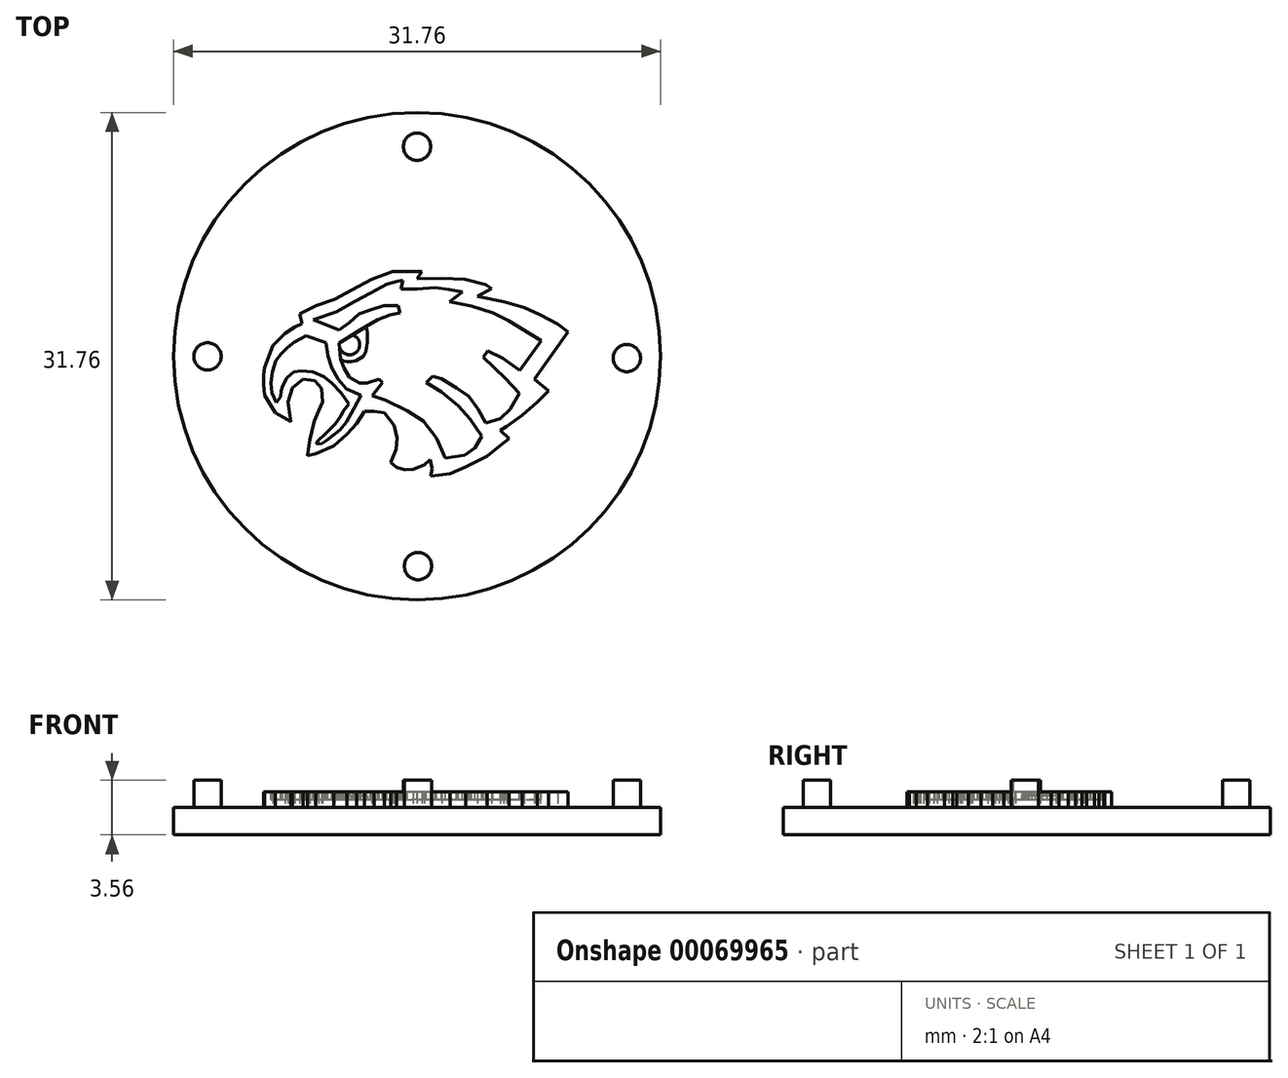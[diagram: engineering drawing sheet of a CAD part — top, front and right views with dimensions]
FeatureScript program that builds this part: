
annotation { "Feature Type Name" : "Feature", "Feature Type Description" : "" }
export const myFeature = defineFeature(function(context is Context, id is Id, definition is map)
    precondition{}
    {
        {
            var Q0;
            Q0=qCreatedBy(makeId("Top.planeOp"),FACE);
            var sketch = newSketch(context, id + "F0", { "sketchPlane" : qUnion([Q0])});
            skCircle(sketch, "E0", {"center": v(0, 0) * mm, "radius": 15.88 * mm});
            skSolve(sketch);
        }
        {
            var Q0;
            Q0=qSketchRegion(id+"F0",true);
            extrude(context, id + "F1", {"entities" : qUnion([Q0]), "oppositeDirection" : true, "depth" : 1.78 * mm});
        }
        {
            var Q0;
            Q0=makeQuery(id+"F1.opExtrude","CAP_FACE",FACE,{"disambiguationData":[OSD([sQuery(id+"F0.wireOp",EDGE,"E0")])],"isStart":true});
            var sketch = newSketch(context, id + "F2", { "sketchPlane" : qUnion([Q0])});
            skCircle(sketch, "E1", {"center": v(0, 0) * mm, "radius": 12.7 * mm});
            skSolve(sketch);
        }
        {
            var Q0;
            Q0=makeQuery(id+"F2.imprint","IMPRINT",FACE,{"disambiguationData":[TD([[makeQuery(id+"F2.imprint","IMPRINT",EDGE,{"derivedFrom":sQuery(id+"F2.wireOp",EDGE,"E1")}),-1.0]])]});
            var sketch = newSketch(context, id + "F3", { "sketchPlane" : qUnion([Q0])});
            skCircle(sketch, "E2", {"center": v(0, 13.65) * mm, "radius": 0.89 * mm});
            skCircle(sketch, "E3", {"center": v(-13.66, -0.02) * mm, "radius": 0.89 * mm});
            skCircle(sketch, "E4", {"center": v(0.06, -13.68) * mm, "radius": 0.89 * mm});
            skCircle(sketch, "E5", {"center": v(13.67, -0.12) * mm, "radius": 0.89 * mm});
            skSolve(sketch);
        }
        {
            var Q0;
            Q0=qSketchRegion(id+"F3",true);
            extrude(context, id + "F4", {"entities" : qUnion([Q0]), "operationType" : NewBodyOperationType.ADD, "depth" : 1.78 * mm});
        }
        {
            var Q0;
            Q0=makeQuery(id+"F2.imprint","IMPRINT",FACE,{"disambiguationData":[TD([[makeQuery(id+"F2.imprint","IMPRINT",EDGE,{"derivedFrom":sQuery(id+"F2.wireOp",EDGE,"E1")}),-1.0]])]});
            var sketch = newSketch(context, id + "F5", { "sketchPlane" : qUnion([Q0])});
            skLineSegment(sketch, "E6", {"start": v(-8.24, -4.25) * mm, "end": v(-9.25, -3.7) * mm});
            skLineSegment(sketch, "E7", {"start": v(-9.25, -3.7) * mm, "end": v(-9.93, -2.55) * mm});
            skLineSegment(sketch, "E8", {"start": v(-9.93, -2.55) * mm, "end": v(-10, -1.84) * mm});
            skLineSegment(sketch, "E9", {"start": v(-10, -1.22) * mm, "end": v(-9.93, -0.75) * mm});
            skLineSegment(sketch, "E10", {"start": v(-9.93, -0.75) * mm, "end": v(-9.42, 0.69) * mm});
            skLineSegment(sketch, "E11", {"start": v(-9.42, 0.69) * mm, "end": v(-8.6, 1.5) * mm});
            skLineSegment(sketch, "E12", {"start": v(-8.6, 1.5) * mm, "end": v(-7.97, 1.88) * mm});
            skLineSegment(sketch, "E13", {"start": v(-7.97, 1.88) * mm, "end": v(-7.5, 2.11) * mm});
            skLineSegment(sketch, "E14", {"start": v(-7.5, 2.11) * mm, "end": v(-7.66, 2.74) * mm});
            skLineSegment(sketch, "E15", {"start": v(-7.66, 2.74) * mm, "end": v(-6.58, 3.29) * mm});
            skLineSegment(sketch, "E16", {"start": v(-6.58, 3.29) * mm, "end": v(-5.36, 3.7) * mm});
            skLineSegment(sketch, "E17", {"start": v(-5.36, 3.7) * mm, "end": v(-4.25, 4.3) * mm});
            skLineSegment(sketch, "E18", {"start": v(-4.25, 4.3) * mm, "end": v(-2.97, 5.01) * mm});
            skLineSegment(sketch, "E19", {"start": v(-2.97, 5.01) * mm, "end": v(-1.58, 5.52) * mm});
            skLineSegment(sketch, "E20", {"start": v(-1.58, 5.52) * mm, "end": v(-1.4, 5.52) * mm});
            skLineSegment(sketch, "E21", {"start": v(-1.4, 5.52) * mm, "end": v(0, 5.52) * mm});
            skLineSegment(sketch, "E22", {"start": v(-0.55, 5.52) * mm, "end": v(0, 5.52) * mm});
            skLineSegment(sketch, "E23", {"start": v(-0.55, 5.52) * mm, "end": v(0.33, 5.52) * mm});
            skLineSegment(sketch, "E24", {"start": v(0.33, 5.52) * mm, "end": v(0, 5.04) * mm});
            skLineSegment(sketch, "E25", {"start": v(0, 5.04) * mm, "end": v(1.62, 5.08) * mm});
            skLineSegment(sketch, "E26", {"start": v(1.62, 5.08) * mm, "end": v(3.1, 5.01) * mm});
            skLineSegment(sketch, "E27", {"start": v(3.1, 5.01) * mm, "end": v(4.46, 4.67) * mm});
            skLineSegment(sketch, "E28", {"start": v(4.46, 4.67) * mm, "end": v(4.87, 4.4) * mm});
            skLineSegment(sketch, "E29", {"start": v(4.87, 4.4) * mm, "end": v(3.92, 3.9) * mm});
            skLineSegment(sketch, "E30", {"start": v(3.92, 3.9) * mm, "end": v(5.64, 3.56) * mm});
            skLineSegment(sketch, "E31", {"start": v(5.64, 3.56) * mm, "end": v(7, 3.15) * mm});
            skLineSegment(sketch, "E32", {"start": v(7, 3.15) * mm, "end": v(8.04, 2.68) * mm});
            skLineSegment(sketch, "E33", {"start": v(8.04, 2.68) * mm, "end": v(9.19, 2.07) * mm});
            skLineSegment(sketch, "E34", {"start": v(9.19, 2.07) * mm, "end": v(9.83, 1.57) * mm});
            skLineSegment(sketch, "E35", {"start": v(9.83, 1.57) * mm, "end": v(7.63, -1.5) * mm});
            skLineSegment(sketch, "E36", {"start": v(7.63, -1.5) * mm, "end": v(8.58, -2.25) * mm});
            skLineSegment(sketch, "E37", {"start": v(8.58, -2.25) * mm, "end": v(7.84, -3) * mm});
            skLineSegment(sketch, "E38", {"start": v(7.84, -3) * mm, "end": v(6.86, -3.83) * mm});
            skLineSegment(sketch, "E39", {"start": v(6.86, -3.83) * mm, "end": v(5.84, -4.58) * mm});
            skLineSegment(sketch, "E40", {"start": v(5.84, -4.58) * mm, "end": v(5.44, -4.85) * mm});
            skLineSegment(sketch, "E41", {"start": v(5.44, -4.85) * mm, "end": v(6.01, -5.39) * mm});
            skLineSegment(sketch, "E42", {"start": v(6.01, -5.39) * mm, "end": v(5.44, -5.83) * mm});
            skLineSegment(sketch, "E43", {"start": v(5.44, -5.83) * mm, "end": v(4.56, -6.5) * mm});
            skLineSegment(sketch, "E44", {"start": v(4.56, -6.5) * mm, "end": v(3.18, -7.21) * mm});
            skLineSegment(sketch, "E45", {"start": v(3.18, -7.21) * mm, "end": v(2.16, -7.65) * mm});
            skLineSegment(sketch, "E46", {"start": v(2.16, -7.65) * mm, "end": v(0.88, -7.82) * mm});
            skLineSegment(sketch, "E47", {"start": v(0.88, -7.82) * mm, "end": v(0.98, -7.35) * mm});
            skLineSegment(sketch, "E48", {"start": v(0.98, -7.35) * mm, "end": v(0.85, -6.74) * mm});
            skLineSegment(sketch, "E49", {"start": v(0.85, -6.74) * mm, "end": v(0.48, -7.08) * mm});
            skLineSegment(sketch, "E50", {"start": v(0.48, -7.08) * mm, "end": v(-0.27, -7.38) * mm});
            skLineSegment(sketch, "E51", {"start": v(-0.27, -7.38) * mm, "end": v(-0.8, -7.41) * mm});
            skLineSegment(sketch, "E52", {"start": v(-0.8, -7.41) * mm, "end": v(-1.35, -7.24) * mm});
            skLineSegment(sketch, "E53", {"start": v(-1.35, -7.24) * mm, "end": v(-1.72, -6.94) * mm});
            skLineSegment(sketch, "E54", {"start": v(-1.72, -6.94) * mm, "end": v(-1.38, -6.06) * mm});
            skLineSegment(sketch, "E55", {"start": v(-1.38, -6.06) * mm, "end": v(-1.31, -5.35) * mm});
            skLineSegment(sketch, "E56", {"start": v(-1.31, -5.35) * mm, "end": v(-1.48, -4.5) * mm});
            skLineSegment(sketch, "E57", {"start": v(-1.48, -4.5) * mm, "end": v(-2.12, -3.7) * mm});
            skLineSegment(sketch, "E58", {"start": v(-2.12, -3.7) * mm, "end": v(-2.8, -3.6) * mm});
            skLineSegment(sketch, "E59", {"start": v(-2.8, -3.6) * mm, "end": v(-3.44, -3.6) * mm});
            skLineSegment(sketch, "E60", {"start": v(-3.44, -3.6) * mm, "end": v(-3.95, -4.37) * mm});
            skLineSegment(sketch, "E61", {"start": v(-3.95, -4.37) * mm, "end": v(-4.59, -5.08) * mm});
            skLineSegment(sketch, "E62", {"start": v(-4.59, -5.08) * mm, "end": v(-5.43, -5.86) * mm});
            skLineSegment(sketch, "E63", {"start": v(-5.43, -5.86) * mm, "end": v(-6.61, -6.37) * mm});
            skLineSegment(sketch, "E64", {"start": v(-6.61, -6.37) * mm, "end": v(-7.15, -6.47) * mm});
            skLineSegment(sketch, "E65", {"start": v(-7.15, -6.47) * mm, "end": v(-6.99, -5.42) * mm});
            skLineSegment(sketch, "E66", {"start": v(-6.99, -5.42) * mm, "end": v(-6.72, -4.24) * mm});
            skLineSegment(sketch, "E67", {"start": v(-6.72, -4.24) * mm, "end": v(-6.41, -3.56) * mm});
            skLineSegment(sketch, "E68", {"start": v(-6.41, -3.56) * mm, "end": v(-6.18, -3) * mm});
            skLineSegment(sketch, "E69", {"start": v(-6.18, -3) * mm, "end": v(-6.2, -2.11) * mm});
            skLineSegment(sketch, "E70", {"start": v(-6.2, -2.11) * mm, "end": v(-6.68, -1.6) * mm});
            skLineSegment(sketch, "E71", {"start": v(-6.68, -1.6) * mm, "end": v(-7.42, -1.5) * mm});
            skLineSegment(sketch, "E72", {"start": v(-7.42, -1.5) * mm, "end": v(-8.13, -2.08) * mm});
            skLineSegment(sketch, "E73", {"start": v(-8.13, -2.08) * mm, "end": v(-8.4, -3) * mm});
            skLineSegment(sketch, "E74", {"start": v(-8.4, -3) * mm, "end": v(-8.3, -3.87) * mm});
            skLineSegment(sketch, "E75", {"start": v(-8.3, -3.87) * mm, "end": v(-8.24, -4.25) * mm});
            skLineSegment(sketch, "E76", {"start": v(-10, -1.22) * mm, "end": v(-10, -1.84) * mm});
            skSolve(sketch);
        }
        {
            var Q0;
            Q0 = qSketchRegion(id + "F5", true);
            extrude(context, id + "F6", {"entities" : qUnion([Q0]), "operationType" : NewBodyOperationType.ADD, "depth" : 1.02 * mm});
        }
        {
            var Q0;
            Q0=makeQuery(id+"F6.opExtrude","CAP_FACE",FACE,{"disambiguationData":[OSD([sQuery(id+"F5.wireOp",EDGE,"E6"),sQuery(id+"F5.wireOp",EDGE,"E7"),sQuery(id+"F5.wireOp",EDGE,"E8"),sQuery(id+"F5.wireOp",EDGE,"E9"),sQuery(id+"F5.wireOp",EDGE,"E10"),sQuery(id+"F5.wireOp",EDGE,"E11"),sQuery(id+"F5.wireOp",EDGE,"E12"),sQuery(id+"F5.wireOp",EDGE,"E13"),sQuery(id+"F5.wireOp",EDGE,"E14"),sQuery(id+"F5.wireOp",EDGE,"E15"),sQuery(id+"F5.wireOp",EDGE,"E16"),sQuery(id+"F5.wireOp",EDGE,"E17"),sQuery(id+"F5.wireOp",EDGE,"E18"),sQuery(id+"F5.wireOp",EDGE,"E19"),sQuery(id+"F5.wireOp",EDGE,"E20"),sQuery(id+"F5.wireOp",EDGE,"E21"),sQuery(id+"F5.wireOp",EDGE,"E23"),sQuery(id+"F5.wireOp",EDGE,"E24"),sQuery(id+"F5.wireOp",EDGE,"E25"),sQuery(id+"F5.wireOp",EDGE,"E26"),sQuery(id+"F5.wireOp",EDGE,"E27"),sQuery(id+"F5.wireOp",EDGE,"E28"),sQuery(id+"F5.wireOp",EDGE,"E29"),sQuery(id+"F5.wireOp",EDGE,"E30"),sQuery(id+"F5.wireOp",EDGE,"E31"),sQuery(id+"F5.wireOp",EDGE,"E32"),sQuery(id+"F5.wireOp",EDGE,"E33"),sQuery(id+"F5.wireOp",EDGE,"E34"),sQuery(id+"F5.wireOp",EDGE,"E35"),sQuery(id+"F5.wireOp",EDGE,"E36"),sQuery(id+"F5.wireOp",EDGE,"E37"),sQuery(id+"F5.wireOp",EDGE,"E38"),sQuery(id+"F5.wireOp",EDGE,"E39"),sQuery(id+"F5.wireOp",EDGE,"E40"),sQuery(id+"F5.wireOp",EDGE,"E41"),sQuery(id+"F5.wireOp",EDGE,"E42"),sQuery(id+"F5.wireOp",EDGE,"E43"),sQuery(id+"F5.wireOp",EDGE,"E44"),sQuery(id+"F5.wireOp",EDGE,"E45"),sQuery(id+"F5.wireOp",EDGE,"E46"),sQuery(id+"F5.wireOp",EDGE,"E47"),sQuery(id+"F5.wireOp",EDGE,"E48"),sQuery(id+"F5.wireOp",EDGE,"E49"),sQuery(id+"F5.wireOp",EDGE,"E50"),sQuery(id+"F5.wireOp",EDGE,"E51"),sQuery(id+"F5.wireOp",EDGE,"E52"),sQuery(id+"F5.wireOp",EDGE,"E53"),sQuery(id+"F5.wireOp",EDGE,"E54"),sQuery(id+"F5.wireOp",EDGE,"E55"),sQuery(id+"F5.wireOp",EDGE,"E56"),sQuery(id+"F5.wireOp",EDGE,"E57"),sQuery(id+"F5.wireOp",EDGE,"E58"),sQuery(id+"F5.wireOp",EDGE,"E59"),sQuery(id+"F5.wireOp",EDGE,"E60"),sQuery(id+"F5.wireOp",EDGE,"E61"),sQuery(id+"F5.wireOp",EDGE,"E62"),sQuery(id+"F5.wireOp",EDGE,"E63"),sQuery(id+"F5.wireOp",EDGE,"E64"),sQuery(id+"F5.wireOp",EDGE,"E65"),sQuery(id+"F5.wireOp",EDGE,"E66"),sQuery(id+"F5.wireOp",EDGE,"E67"),sQuery(id+"F5.wireOp",EDGE,"E68"),sQuery(id+"F5.wireOp",EDGE,"E69"),sQuery(id+"F5.wireOp",EDGE,"E70"),sQuery(id+"F5.wireOp",EDGE,"E71"),sQuery(id+"F5.wireOp",EDGE,"E72"),sQuery(id+"F5.wireOp",EDGE,"E73"),sQuery(id+"F5.wireOp",EDGE,"E74"),sQuery(id+"F5.wireOp",EDGE,"E75"),sQuery(id+"F5.wireOp",EDGE,"E76")])],"isStart":false});
            var sketch = newSketch(context, id + "F7", { "sketchPlane" : qUnion([Q0])});
            skLineSegment(sketch, "E77", {"start": v(8.1, 1) * mm, "end": v(6.7, -0.93) * mm});
            skLineSegment(sketch, "E78", {"start": v(6.7, -0.93) * mm, "end": v(5.58, -0.15) * mm});
            skLineSegment(sketch, "E79", {"start": v(5.58, -0.15) * mm, "end": v(4.6, 0.35) * mm});
            skLineSegment(sketch, "E80", {"start": v(4.6, 0.35) * mm, "end": v(4.3, -0.07) * mm});
            skLineSegment(sketch, "E81", {"start": v(4.3, -0.07) * mm, "end": v(5.75, -1.42) * mm});
            skLineSegment(sketch, "E82", {"start": v(5.75, -1.42) * mm, "end": v(6.65, -2.4) * mm});
            skLineSegment(sketch, "E83", {"start": v(6.65, -2.4) * mm, "end": v(6.08, -3.48) * mm});
            skLineSegment(sketch, "E84", {"start": v(6.08, -3.48) * mm, "end": v(5.42, -4.05) * mm});
            skLineSegment(sketch, "E85", {"start": v(5.42, -4.05) * mm, "end": v(4.47, -4.34) * mm});
            skLineSegment(sketch, "E86", {"start": v(4.47, -4.34) * mm, "end": v(3.98, -3.44) * mm});
            skLineSegment(sketch, "E87", {"start": v(3.98, -3.44) * mm, "end": v(3.36, -2.62) * mm});
            skLineSegment(sketch, "E88", {"start": v(3.36, -2.62) * mm, "end": v(2.58, -2.08) * mm});
            skLineSegment(sketch, "E89", {"start": v(2.58, -2.08) * mm, "end": v(1.6, -1.46) * mm});
            skLineSegment(sketch, "E90", {"start": v(1.6, -1.46) * mm, "end": v(1.02, -1.3) * mm});
            skLineSegment(sketch, "E91", {"start": v(1.02, -1.3) * mm, "end": v(0.6, -1.71) * mm});
            skLineSegment(sketch, "E92", {"start": v(0.6, -1.71) * mm, "end": v(1.6, -2.33) * mm});
            skLineSegment(sketch, "E93", {"start": v(1.6, -2.33) * mm, "end": v(2.7, -3.23) * mm});
            skLineSegment(sketch, "E94", {"start": v(2.7, -3.23) * mm, "end": v(3.44, -4.1) * mm});
            skLineSegment(sketch, "E95", {"start": v(3.44, -4.1) * mm, "end": v(4.22, -5.2) * mm});
            skLineSegment(sketch, "E96", {"start": v(4.22, -5.2) * mm, "end": v(3.77, -5.99) * mm});
            skLineSegment(sketch, "E97", {"start": v(3.77, -5.99) * mm, "end": v(3.11, -6.44) * mm});
            skLineSegment(sketch, "E98", {"start": v(3.11, -6.44) * mm, "end": v(1.84, -6.64) * mm});
            skLineSegment(sketch, "E99", {"start": v(1.84, -6.64) * mm, "end": v(1.26, -5.33) * mm});
            skLineSegment(sketch, "E100", {"start": v(1.26, -5.33) * mm, "end": v(0.4, -4.22) * mm});
            skLineSegment(sketch, "E101", {"start": v(0.4, -4.22) * mm, "end": v(-0.63, -3.56) * mm});
            skLineSegment(sketch, "E102", {"start": v(-0.63, -3.56) * mm, "end": v(-2.07, -2.86) * mm});
            skLineSegment(sketch, "E103", {"start": v(-2.07, -2.86) * mm, "end": v(-2.93, -2.57) * mm});
            skLineSegment(sketch, "E104", {"start": v(-2.93, -2.57) * mm, "end": v(-2.27, -1.71) * mm});
            skLineSegment(sketch, "E105", {"start": v(-2.27, -1.71) * mm, "end": v(-2.48, -1.5) * mm});
            skLineSegment(sketch, "E106", {"start": v(-2.48, -1.5) * mm, "end": v(-3.26, -1.75) * mm});
            skLineSegment(sketch, "E107", {"start": v(-3.26, -1.75) * mm, "end": v(-3.75, -1.75) * mm});
            skLineSegment(sketch, "E108", {"start": v(-3.75, -1.75) * mm, "end": v(-4.41, -1.38) * mm});
            skLineSegment(sketch, "E109", {"start": v(-4.41, -1.38) * mm, "end": v(-4.78, -0.76) * mm});
            skLineSegment(sketch, "E110", {"start": v(-4.78, -0.76) * mm, "end": v(-4.99, -0.19) * mm});
            skLineSegment(sketch, "E111", {"start": v(-4.99, -0.19) * mm, "end": v(-5.07, 0.84) * mm});
            skLineSegment(sketch, "E112", {"start": v(-5.07, 0.84) * mm, "end": v(-3.71, 1.7) * mm});
            skLineSegment(sketch, "E113", {"start": v(-3.71, 1.7) * mm, "end": v(-2.56, 2.36) * mm});
            skLineSegment(sketch, "E114", {"start": v(-2.56, 2.36) * mm, "end": v(-1.74, 2.69) * mm});
            skLineSegment(sketch, "E115", {"start": v(-1.74, 2.69) * mm, "end": v(-1.12, 2.81) * mm});
            skLineSegment(sketch, "E116", {"start": v(-1.12, 2.81) * mm, "end": v(-1.24, 3.3) * mm});
            skLineSegment(sketch, "E117", {"start": v(-1.24, 3.3) * mm, "end": v(-2.15, 3.3) * mm});
            skLineSegment(sketch, "E118", {"start": v(-2.15, 3.3) * mm, "end": v(-3.05, 3.02) * mm});
            skLineSegment(sketch, "E119", {"start": v(-3.05, 3.02) * mm, "end": v(-3.8, 2.77) * mm});
            skLineSegment(sketch, "E120", {"start": v(-3.8, 2.77) * mm, "end": v(-4.41, 2.2) * mm});
            skLineSegment(sketch, "E121", {"start": v(-4.41, 2.2) * mm, "end": v(-5.07, 1.7) * mm});
            skLineSegment(sketch, "E122", {"start": v(-5.07, 1.7) * mm, "end": v(-6.75, 2.36) * mm});
            skLineSegment(sketch, "E123", {"start": v(-6.75, 2.36) * mm, "end": v(-5.27, 2.9) * mm});
            skLineSegment(sketch, "E124", {"start": v(-5.27, 2.9) * mm, "end": v(-4.04, 3.6) * mm});
            skLineSegment(sketch, "E125", {"start": v(-4.04, 3.6) * mm, "end": v(-3.01, 4.13) * mm});
            skLineSegment(sketch, "E126", {"start": v(-3.01, 4.13) * mm, "end": v(-1.98, 4.7) * mm});
            skLineSegment(sketch, "E127", {"start": v(-1.98, 4.7) * mm, "end": v(-1.29, 4.87) * mm});
            skLineSegment(sketch, "E128", {"start": v(-1.29, 4.87) * mm, "end": v(-0.92, 4.95) * mm});
            skLineSegment(sketch, "E129", {"start": v(-0.92, 4.95) * mm, "end": v(-1.04, 4.38) * mm});
            skLineSegment(sketch, "E130", {"start": v(-1.04, 4.38) * mm, "end": v(-0.01, 4.38) * mm});
            skLineSegment(sketch, "E131", {"start": v(-0.01, 4.38) * mm, "end": v(1.18, 4.46) * mm});
            skLineSegment(sketch, "E132", {"start": v(1.18, 4.46) * mm, "end": v(2.09, 4.33) * mm});
            skLineSegment(sketch, "E133", {"start": v(2.09, 4.33) * mm, "end": v(2.95, 4.17) * mm});
            skLineSegment(sketch, "E134", {"start": v(2.95, 4.17) * mm, "end": v(2.13, 3.55) * mm});
            skLineSegment(sketch, "E135", {"start": v(2.13, 3.55) * mm, "end": v(3.57, 3.26) * mm});
            skLineSegment(sketch, "E136", {"start": v(3.57, 3.26) * mm, "end": v(4.97, 2.81) * mm});
            skLineSegment(sketch, "E137", {"start": v(4.97, 2.81) * mm, "end": v(5.95, 2.32) * mm});
            skLineSegment(sketch, "E138", {"start": v(5.95, 2.32) * mm, "end": v(7.35, 1.46) * mm});
            skLineSegment(sketch, "E139", {"start": v(7.35, 1.46) * mm, "end": v(8.1, 1) * mm});
            skSolve(sketch);
        }
        {
            var Q0;
            Q0 = qSketchRegion(id + "F7", true);
            extrude(context, id + "F8", {"entities" : qUnion([Q0]), "operationType" : NewBodyOperationType.REMOVE, "oppositeDirection" : true, "depth" : 0.5 * mm});
        }
        {
            var Q0;
            Q0=makeQuery(id+"F6.opExtrude","CAP_FACE",FACE,{"disambiguationData":[OSD([sQuery(id+"F5.wireOp",EDGE,"E6"),sQuery(id+"F5.wireOp",EDGE,"E7"),sQuery(id+"F5.wireOp",EDGE,"E8"),sQuery(id+"F5.wireOp",EDGE,"E9"),sQuery(id+"F5.wireOp",EDGE,"E10"),sQuery(id+"F5.wireOp",EDGE,"E11"),sQuery(id+"F5.wireOp",EDGE,"E12"),sQuery(id+"F5.wireOp",EDGE,"E13"),sQuery(id+"F5.wireOp",EDGE,"E14"),sQuery(id+"F5.wireOp",EDGE,"E15"),sQuery(id+"F5.wireOp",EDGE,"E16"),sQuery(id+"F5.wireOp",EDGE,"E17"),sQuery(id+"F5.wireOp",EDGE,"E18"),sQuery(id+"F5.wireOp",EDGE,"E19"),sQuery(id+"F5.wireOp",EDGE,"E20"),sQuery(id+"F5.wireOp",EDGE,"E21"),sQuery(id+"F5.wireOp",EDGE,"E23"),sQuery(id+"F5.wireOp",EDGE,"E24"),sQuery(id+"F5.wireOp",EDGE,"E25"),sQuery(id+"F5.wireOp",EDGE,"E26"),sQuery(id+"F5.wireOp",EDGE,"E27"),sQuery(id+"F5.wireOp",EDGE,"E28"),sQuery(id+"F5.wireOp",EDGE,"E29"),sQuery(id+"F5.wireOp",EDGE,"E30"),sQuery(id+"F5.wireOp",EDGE,"E31"),sQuery(id+"F5.wireOp",EDGE,"E32"),sQuery(id+"F5.wireOp",EDGE,"E33"),sQuery(id+"F5.wireOp",EDGE,"E34"),sQuery(id+"F5.wireOp",EDGE,"E35"),sQuery(id+"F5.wireOp",EDGE,"E36"),sQuery(id+"F5.wireOp",EDGE,"E37"),sQuery(id+"F5.wireOp",EDGE,"E38"),sQuery(id+"F5.wireOp",EDGE,"E39"),sQuery(id+"F5.wireOp",EDGE,"E40"),sQuery(id+"F5.wireOp",EDGE,"E41"),sQuery(id+"F5.wireOp",EDGE,"E42"),sQuery(id+"F5.wireOp",EDGE,"E43"),sQuery(id+"F5.wireOp",EDGE,"E44"),sQuery(id+"F5.wireOp",EDGE,"E45"),sQuery(id+"F5.wireOp",EDGE,"E46"),sQuery(id+"F5.wireOp",EDGE,"E47"),sQuery(id+"F5.wireOp",EDGE,"E48"),sQuery(id+"F5.wireOp",EDGE,"E49"),sQuery(id+"F5.wireOp",EDGE,"E50"),sQuery(id+"F5.wireOp",EDGE,"E51"),sQuery(id+"F5.wireOp",EDGE,"E52"),sQuery(id+"F5.wireOp",EDGE,"E53"),sQuery(id+"F5.wireOp",EDGE,"E54"),sQuery(id+"F5.wireOp",EDGE,"E55"),sQuery(id+"F5.wireOp",EDGE,"E56"),sQuery(id+"F5.wireOp",EDGE,"E57"),sQuery(id+"F5.wireOp",EDGE,"E58"),sQuery(id+"F5.wireOp",EDGE,"E59"),sQuery(id+"F5.wireOp",EDGE,"E60"),sQuery(id+"F5.wireOp",EDGE,"E61"),sQuery(id+"F5.wireOp",EDGE,"E62"),sQuery(id+"F5.wireOp",EDGE,"E63"),sQuery(id+"F5.wireOp",EDGE,"E64"),sQuery(id+"F5.wireOp",EDGE,"E65"),sQuery(id+"F5.wireOp",EDGE,"E66"),sQuery(id+"F5.wireOp",EDGE,"E67"),sQuery(id+"F5.wireOp",EDGE,"E68"),sQuery(id+"F5.wireOp",EDGE,"E69"),sQuery(id+"F5.wireOp",EDGE,"E70"),sQuery(id+"F5.wireOp",EDGE,"E71"),sQuery(id+"F5.wireOp",EDGE,"E72"),sQuery(id+"F5.wireOp",EDGE,"E73"),sQuery(id+"F5.wireOp",EDGE,"E74"),sQuery(id+"F5.wireOp",EDGE,"E75"),sQuery(id+"F5.wireOp",EDGE,"E76")])],"isStart":false});
            var sketch = newSketch(context, id + "F9", { "sketchPlane" : qUnion([Q0])});
            skLineSegment(sketch, "E140", {"start": v(-8.89, -2.66) * mm, "end": v(-9.18, -3.02) * mm});
            skLineSegment(sketch, "E141", {"start": v(-9.18, -3.02) * mm, "end": v(-9.47, -2.38) * mm});
            skLineSegment(sketch, "E142", {"start": v(-9.47, -2.38) * mm, "end": v(-9.53, -1.76) * mm});
            skLineSegment(sketch, "E143", {"start": v(-9.53, -1.76) * mm, "end": v(-9.43, -1.02) * mm});
            skLineSegment(sketch, "E144", {"start": v(-9.43, -1.02) * mm, "end": v(-9.2, -0.29) * mm});
            skLineSegment(sketch, "E145", {"start": v(-9.2, -0.29) * mm, "end": v(-8.85, 0.16) * mm});
            skLineSegment(sketch, "E146", {"start": v(-8.85, 0.16) * mm, "end": v(-8.46, 0.57) * mm});
            skLineSegment(sketch, "E147", {"start": v(-8.46, 0.57) * mm, "end": v(-8, 0.92) * mm});
            skLineSegment(sketch, "E148", {"start": v(-8, 0.92) * mm, "end": v(-7.6, 1.13) * mm});
            skLineSegment(sketch, "E149", {"start": v(-7.6, 1.13) * mm, "end": v(-7.26, 1.32) * mm});
            skLineSegment(sketch, "E150", {"start": v(-7.26, 1.32) * mm, "end": v(-5.94, 0.88) * mm});
            skLineSegment(sketch, "E151", {"start": v(-5.94, 0.88) * mm, "end": v(-5.8, 0.02) * mm});
            skLineSegment(sketch, "E152", {"start": v(-5.8, 0.02) * mm, "end": v(-5.57, -0.75) * mm});
            skLineSegment(sketch, "E153", {"start": v(-5.57, -0.75) * mm, "end": v(-5.16, -1.51) * mm});
            skLineSegment(sketch, "E154", {"start": v(-5.16, -1.51) * mm, "end": v(-4.62, -2.13) * mm});
            skLineSegment(sketch, "E155", {"start": v(-4.62, -2.13) * mm, "end": v(-3.67, -2.56) * mm});
            skLineSegment(sketch, "E156", {"start": v(-3.67, -2.56) * mm, "end": v(-4.13, -3.45) * mm});
            skLineSegment(sketch, "E157", {"start": v(-4.13, -3.45) * mm, "end": v(-4.62, -4.29) * mm});
            skLineSegment(sketch, "E158", {"start": v(-4.62, -4.29) * mm, "end": v(-5.02, -4.8) * mm});
            skLineSegment(sketch, "E159", {"start": v(-5.02, -4.8) * mm, "end": v(-5.9, -5.5) * mm});
            skLineSegment(sketch, "E160", {"start": v(-5.9, -5.5) * mm, "end": v(-6.2, -5.7) * mm});
            skLineSegment(sketch, "E161", {"start": v(-4.83, -3.6) * mm, "end": v(-4.44, -3.12) * mm});
            skLineSegment(sketch, "E162", {"start": v(-4.44, -3.12) * mm, "end": v(-4.95, -2.4) * mm});
            skLineSegment(sketch, "E163", {"start": v(-4.95, -2.4) * mm, "end": v(-5.55, -1.76) * mm});
            skLineSegment(sketch, "E164", {"start": v(-5.55, -1.76) * mm, "end": v(-6.05, -1.34) * mm});
            skLineSegment(sketch, "E165", {"start": v(-6.05, -1.34) * mm, "end": v(-6.81, -1.02) * mm});
            skLineSegment(sketch, "E166", {"start": v(-6.81, -1.02) * mm, "end": v(-7.55, -0.95) * mm});
            skLineSegment(sketch, "E167", {"start": v(-7.55, -0.95) * mm, "end": v(-8.03, -1.02) * mm});
            skLineSegment(sketch, "E168", {"start": v(-8.03, -1.02) * mm, "end": v(-8.48, -1.4) * mm});
            skLineSegment(sketch, "E169", {"start": v(-8.48, -1.4) * mm, "end": v(-8.75, -1.96) * mm});
            skLineSegment(sketch, "E170", {"start": v(-8.75, -1.96) * mm, "end": v(-8.85, -2.27) * mm});
            skLineSegment(sketch, "E171", {"start": v(-8.85, -2.27) * mm, "end": v(-8.89, -2.66) * mm});
            skLineSegment(sketch, "E172", {"start": v(-6.46, -5.5) * mm, "end": v(-5.98, -5.06) * mm});
            skLineSegment(sketch, "E173", {"start": v(-5.98, -5.06) * mm, "end": v(-5.34, -4.42) * mm});
            skLineSegment(sketch, "E174", {"start": v(-5.34, -4.42) * mm, "end": v(-4.97, -3.88) * mm});
            skLineSegment(sketch, "E175", {"start": v(-4.97, -3.88) * mm, "end": v(-4.83, -3.6) * mm});
            skLineSegment(sketch, "E176", {"start": v(-6.2, -5.7) * mm, "end": v(-6.59, -5.72) * mm});
            skLineSegment(sketch, "E177", {"start": v(-6.59, -5.72) * mm, "end": v(-6.46, -5.5) * mm});
            skSolve(sketch);
        }
        {
            var Q0;
            Q0 = qSketchRegion(id + "F9", true);
            extrude(context, id + "F10", {"entities" : qUnion([Q0]), "operationType" : NewBodyOperationType.REMOVE, "oppositeDirection" : true, "depth" : 0.5 * mm});
        }
        {
            var Q0;
            Q0=makeQuery(id+"F8.boolean.opBoolean","COPY",FACE,{"derivedFrom":makeQuery(id+"F8.opExtrude","CAP_FACE",FACE,{"disambiguationData":[OSD([sQuery(id+"F7.wireOp",EDGE,"E77"),sQuery(id+"F7.wireOp",EDGE,"E78"),sQuery(id+"F7.wireOp",EDGE,"E79"),sQuery(id+"F7.wireOp",EDGE,"E80"),sQuery(id+"F7.wireOp",EDGE,"E81"),sQuery(id+"F7.wireOp",EDGE,"E82"),sQuery(id+"F7.wireOp",EDGE,"E83"),sQuery(id+"F7.wireOp",EDGE,"E84"),sQuery(id+"F7.wireOp",EDGE,"E85"),sQuery(id+"F7.wireOp",EDGE,"E86"),sQuery(id+"F7.wireOp",EDGE,"E87"),sQuery(id+"F7.wireOp",EDGE,"E88"),sQuery(id+"F7.wireOp",EDGE,"E89"),sQuery(id+"F7.wireOp",EDGE,"E90"),sQuery(id+"F7.wireOp",EDGE,"E91"),sQuery(id+"F7.wireOp",EDGE,"E92"),sQuery(id+"F7.wireOp",EDGE,"E93"),sQuery(id+"F7.wireOp",EDGE,"E94"),sQuery(id+"F7.wireOp",EDGE,"E95"),sQuery(id+"F7.wireOp",EDGE,"E96"),sQuery(id+"F7.wireOp",EDGE,"E97"),sQuery(id+"F7.wireOp",EDGE,"E98"),sQuery(id+"F7.wireOp",EDGE,"E99"),sQuery(id+"F7.wireOp",EDGE,"E100"),sQuery(id+"F7.wireOp",EDGE,"E101"),sQuery(id+"F7.wireOp",EDGE,"E102"),sQuery(id+"F7.wireOp",EDGE,"E103"),sQuery(id+"F7.wireOp",EDGE,"E104"),sQuery(id+"F7.wireOp",EDGE,"E105"),sQuery(id+"F7.wireOp",EDGE,"E106"),sQuery(id+"F7.wireOp",EDGE,"E107"),sQuery(id+"F7.wireOp",EDGE,"E108"),sQuery(id+"F7.wireOp",EDGE,"E109"),sQuery(id+"F7.wireOp",EDGE,"E110"),sQuery(id+"F7.wireOp",EDGE,"E111"),sQuery(id+"F7.wireOp",EDGE,"E112"),sQuery(id+"F7.wireOp",EDGE,"E113"),sQuery(id+"F7.wireOp",EDGE,"E114"),sQuery(id+"F7.wireOp",EDGE,"E115"),sQuery(id+"F7.wireOp",EDGE,"E116"),sQuery(id+"F7.wireOp",EDGE,"E117"),sQuery(id+"F7.wireOp",EDGE,"E118"),sQuery(id+"F7.wireOp",EDGE,"E119"),sQuery(id+"F7.wireOp",EDGE,"E120"),sQuery(id+"F7.wireOp",EDGE,"E121"),sQuery(id+"F7.wireOp",EDGE,"E122"),sQuery(id+"F7.wireOp",EDGE,"E123"),sQuery(id+"F7.wireOp",EDGE,"E124"),sQuery(id+"F7.wireOp",EDGE,"E125"),sQuery(id+"F7.wireOp",EDGE,"E126"),sQuery(id+"F7.wireOp",EDGE,"E127"),sQuery(id+"F7.wireOp",EDGE,"E128"),sQuery(id+"F7.wireOp",EDGE,"E129"),sQuery(id+"F7.wireOp",EDGE,"E130"),sQuery(id+"F7.wireOp",EDGE,"E131"),sQuery(id+"F7.wireOp",EDGE,"E132"),sQuery(id+"F7.wireOp",EDGE,"E133"),sQuery(id+"F7.wireOp",EDGE,"E134"),sQuery(id+"F7.wireOp",EDGE,"E135"),sQuery(id+"F7.wireOp",EDGE,"E136"),sQuery(id+"F7.wireOp",EDGE,"E137"),sQuery(id+"F7.wireOp",EDGE,"E138"),sQuery(id+"F7.wireOp",EDGE,"E139")])],"isStart":false})});
            var sketch = newSketch(context, id + "F11", { "sketchPlane" : qUnion([Q0])});
            skLineSegment(sketch, "E178", {"start": v(-5.07, 0.84) * mm, "end": v(-3.31, 1.93) * mm});
            skLineSegment(sketch, "E179", {"start": v(-3.31, 1.93) * mm, "end": v(-3.25, 1.51) * mm});
            skLineSegment(sketch, "E180", {"start": v(-3.25, 1.51) * mm, "end": v(-3.25, 0.9) * mm});
            skLineSegment(sketch, "E181", {"start": v(-3.25, 0.9) * mm, "end": v(-3.33, 0.3) * mm});
            skLineSegment(sketch, "E182", {"start": v(-3.33, 0.3) * mm, "end": v(-3.49, 0) * mm});
            skLineSegment(sketch, "E183", {"start": v(-3.49, 0) * mm, "end": v(-3.97, -0.3) * mm});
            skLineSegment(sketch, "E184", {"start": v(-3.97, -0.3) * mm, "end": v(-4.3, -0.35) * mm});
            skLineSegment(sketch, "E185", {"start": v(-4.3, -0.35) * mm, "end": v(-4.57, -0.35) * mm});
            skLineSegment(sketch, "E186", {"start": v(-4.57, -0.35) * mm, "end": v(-4.75, -0.34) * mm});
            skLineSegment(sketch, "E187", {"start": v(-4.75, -0.34) * mm, "end": v(-4.99, -0.19) * mm});
            skLineSegment(sketch, "E188", {"start": v(-4.99, -0.19) * mm, "end": v(-5.07, 0.84) * mm});
            skSolve(sketch);
        }
        {
            var Q0;
            Q0 = qSketchRegion(id + "F11", true);
            extrude(context, id + "F12", {"entities" : qUnion([Q0]), "depth" : 0.25 * mm});
        }
        {
            var Q0;
            Q0=makeQuery(id+"F12.opExtrude","CAP_FACE",FACE,{"disambiguationData":[OSD([sQuery(id+"F11.wireOp",EDGE,"E178"),sQuery(id+"F11.wireOp",EDGE,"E179"),sQuery(id+"F11.wireOp",EDGE,"E180"),sQuery(id+"F11.wireOp",EDGE,"E181"),sQuery(id+"F11.wireOp",EDGE,"E182"),sQuery(id+"F11.wireOp",EDGE,"E183"),sQuery(id+"F11.wireOp",EDGE,"E184"),sQuery(id+"F11.wireOp",EDGE,"E185"),sQuery(id+"F11.wireOp",EDGE,"E186"),sQuery(id+"F11.wireOp",EDGE,"E187"),sQuery(id+"F11.wireOp",EDGE,"E188")])],"isStart":false});
            var sketch = newSketch(context, id + "F13", { "sketchPlane" : qUnion([Q0])});
            skArc(sketch, "E189", {"start": v(-5.07, 0.84) * mm, "mid": v(-4.05, 0.18) * mm, "end": v(-4.2, 1.38) * mm});
            skLineSegment(sketch, "E190", {"start": v(-5.07, 0.84) * mm, "end": v(-4.2, 1.38) * mm});
            skSolve(sketch);
        }
        {
            var Q0;
            Q0 = qSketchRegion(id + "F13", true);
            extrude(context, id + "F14", {"entities" : qUnion([Q0]), "depth" : 0.16 * mm});
        }
    });
